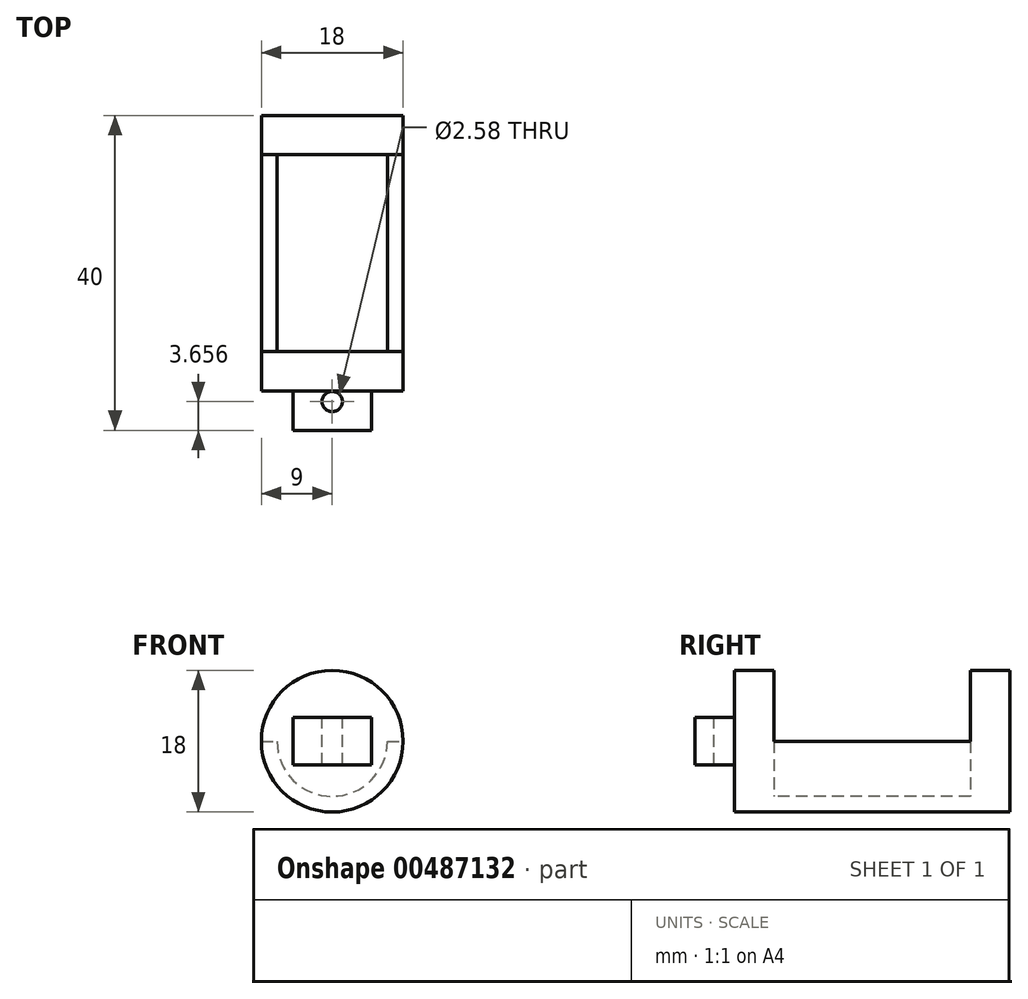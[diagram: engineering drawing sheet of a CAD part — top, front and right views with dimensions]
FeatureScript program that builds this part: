
annotation { "Feature Type Name" : "Feature", "Feature Type Description" : "" }
export const myFeature = defineFeature(function(context is Context, id is Id, definition is map)
    precondition{}
    {
        {
            var Q0;
            Q0=qCreatedBy(makeId("Front.planeOp"),FACE);
            var sketch = newSketch(context, id + "F0", { "sketchPlane" : qUnion([Q0])});
            skCircle(sketch, "E0", {"center": v(0, 0) * mm, "radius": 9 * mm});
            skSolve(sketch);
        }
        {
            var Q0;
            Q0 = qSketchRegion(id + "F0", true);
            extrude(context, id + "F1", {"entities" : qUnion([Q0]), "depth" : 35 * mm});
        }
        {
            var Q0;
            Q0=makeQuery(id+"F1.opExtrude","CAP_FACE",FACE,{"disambiguationData":[OSD([sQuery(id+"F0.wireOp",EDGE,"E0")])],"isStart":false});
            cPlane(context, id + "F2", {"entities" : qUnion([Q0]), "cplaneType" : CPlaneType.OFFSET, "offset" : 5 * mm, "oppositeDirection" : true, "width" : 150 * mm, "height" : 150 * mm});
        }
        {
            var Q0;
            Q0=qCreatedBy(id+"F2.planeOp",FACE);
            var sketch = newSketch(context, id + "F3", { "sketchPlane" : qUnion([Q0])});
            skLineSegment(sketch, "E1.bottom", {"start": v(-10, 0) * mm, "end": v(10, 0) * mm});
            skLineSegment(sketch, "E1.top", {"start": v(-10, 10) * mm, "end": v(10, 10) * mm});
            skLineSegment(sketch, "E1.left", {"start": v(-10, 0) * mm, "end": v(-10, 10) * mm});
            skLineSegment(sketch, "E1.right", {"start": v(10, 0) * mm, "end": v(10, 10) * mm});
            skCircle(sketch, "E2", {"center": v(0, 0) * mm, "radius": 7 * mm});
            skSolve(sketch);
        }
        {
            var Q0;
            Q0 = qSketchRegion(id + "F3", true);
            extrude(context, id + "F4", {"entities" : qUnion([Q0]), "operationType" : NewBodyOperationType.REMOVE, "oppositeDirection" : true, "depth" : 25 * mm});
        }
        {
            var Q0;
            Q0=makeQuery(id+"F1.opExtrude","CAP_FACE",FACE,{"disambiguationData":[OSD([sQuery(id+"F0.wireOp",EDGE,"E0")])],"isStart":false});
            var sketch = newSketch(context, id + "F5", { "sketchPlane" : qUnion([Q0])});
            skLineSegment(sketch, "E3.bottom", {"start": v(-5, 3) * mm, "end": v(5, 3) * mm});
            skLineSegment(sketch, "E3.top", {"start": v(-5, -3) * mm, "end": v(5, -3) * mm});
            skLineSegment(sketch, "E3.left", {"start": v(-5, 3) * mm, "end": v(-5, -3) * mm});
            skLineSegment(sketch, "E3.right", {"start": v(5, 3) * mm, "end": v(5, -3) * mm});
            skSolve(sketch);
        }
        {
            var Q0;
            Q0 = qSketchRegion(id + "F5", true);
            extrude(context, id + "F6", {"entities" : qUnion([Q0]), "operationType" : NewBodyOperationType.ADD, "depth" : 5 * mm});
        }
        {
            var Q0;
            Q0=makeQuery(id+"F6.opExtrude","SWEPT_FACE",FACE,{"disambiguationData":[OSD([sQuery(id+"F5.wireOp",EDGE,"E3.bottom")])]});
            var sketch = newSketch(context, id + "F7", { "sketchPlane" : qUnion([Q0])});
            skCircle(sketch, "E4", {"center": v(0, -36.34) * mm, "radius": 1.3 * mm});
            skSolve(sketch);
        }
        {
            var Q0;
            Q0 = qSketchRegion(id + "F7", true);
            extrude(context, id + "F8", {"entities" : qUnion([Q0]), "operationType" : NewBodyOperationType.REMOVE, "oppositeDirection" : true, "depth" : 25 * mm});
        }
    });
